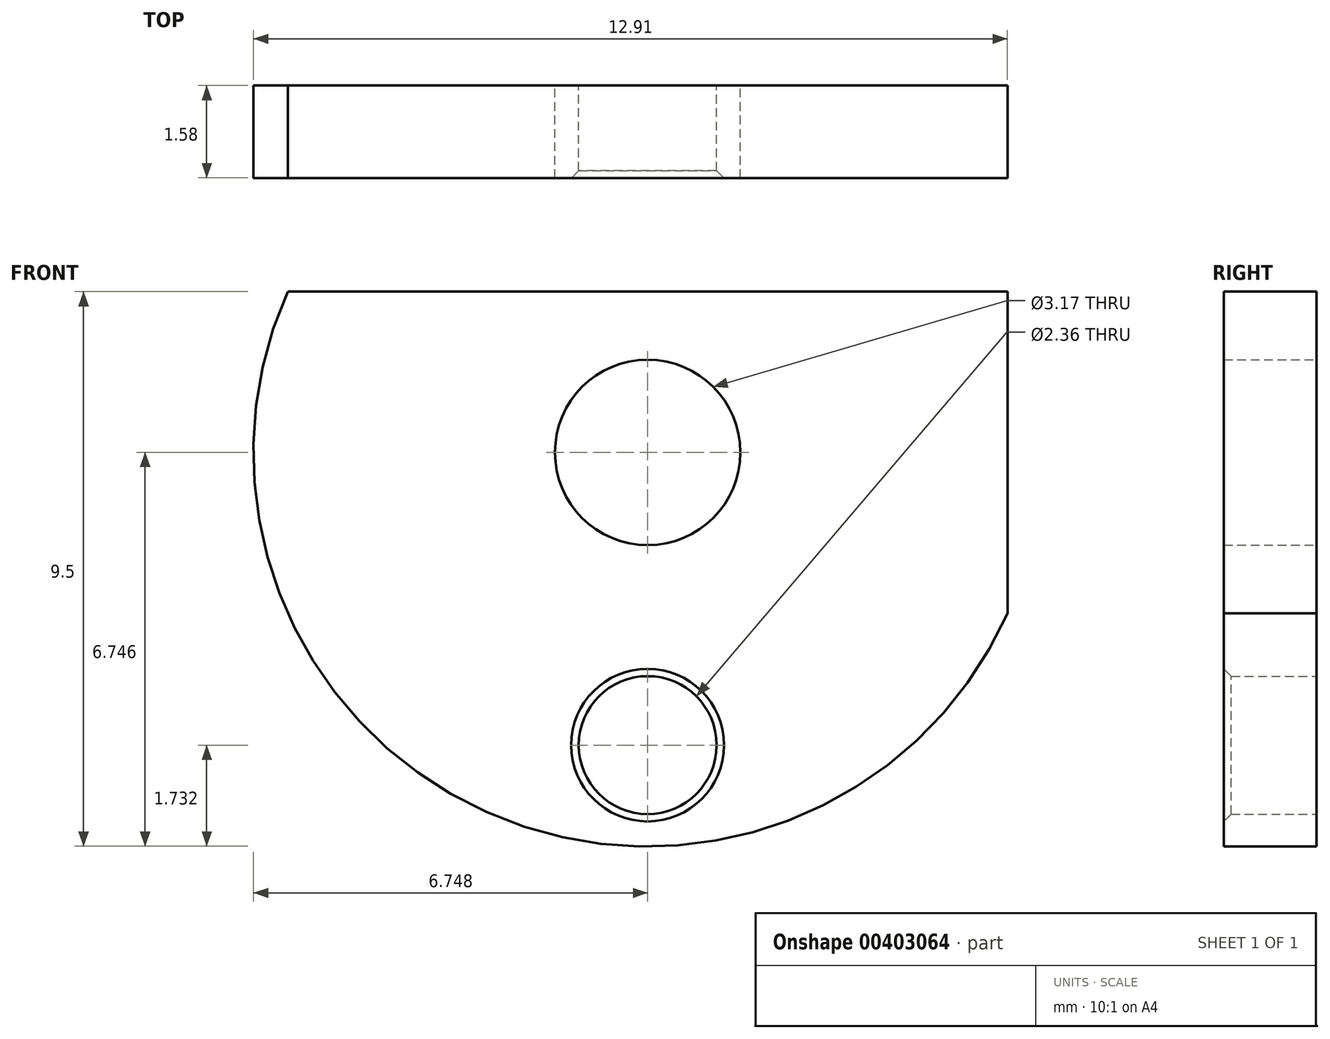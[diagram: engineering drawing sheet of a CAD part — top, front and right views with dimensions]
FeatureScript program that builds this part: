
annotation { "Feature Type Name" : "Feature", "Feature Type Description" : "" }
export const myFeature = defineFeature(function(context is Context, id is Id, definition is map)
    precondition{}
    {
        {
            var Q0;
            Q0=qCreatedBy(makeId("Front.planeOp"),FACE);
            var sketch = newSketch(context, id + "F0", { "sketchPlane" : qUnion([Q0])});
            skArc(sketch, "E0", {"start": v(-7.04, 4) * mm, "mid": v(-3.64, -4.93) * mm, "end": v(5.28, -1.52) * mm});
            skCircle(sketch, "E1", {"center": v(-0.88, 1.24) * mm, "radius": 1.59 * mm});
            skLineSegment(sketch, "E2", {"start": v(-7.04, 4) * mm, "end": v(5.28, 4) * mm});
            skLineSegment(sketch, "E3", {"start": v(5.28, 4) * mm, "end": v(5.28, -1.52) * mm});
            skCircle(sketch, "E4", {"center": v(-0.88, -3.78) * mm, "radius": 1.18 * mm});
            skSolve(sketch);
        }
        {
            var Q0;
            Q0=makeQuery(id+"F0.imprint","IMPRINT",FACE,{"disambiguationData":[TD([[makeQuery(id+"F0.imprint","IMPRINT",EDGE,{"derivedFrom":sQuery(id+"F0.wireOp",EDGE,"E0")}),1.0]])]});
            extrude(context, id + "F1", {"entities" : qUnion([Q0]), "endBound" : BoundingType.SYMMETRIC, "depth" : 1.59 * mm});
        }
        {
            var Q0;
            Q0=makeQuery(id+"F1.opExtrude","CAP_EDGE",EDGE,{"disambiguationData":[OSD([sQuery(id+"F0.wireOp",EDGE,"E4")])],"isStart":false});
            chamfer(context, id + "F2", {"entities" : qUnion([Q0]), "chamferType" : ChamferType.TWO_OFFSETS, "width1" : 0.13 * mm, "oppositeDirection" : false, "width2" : 0.13 * mm, "tangentPropagation" : true});
        }
    });
